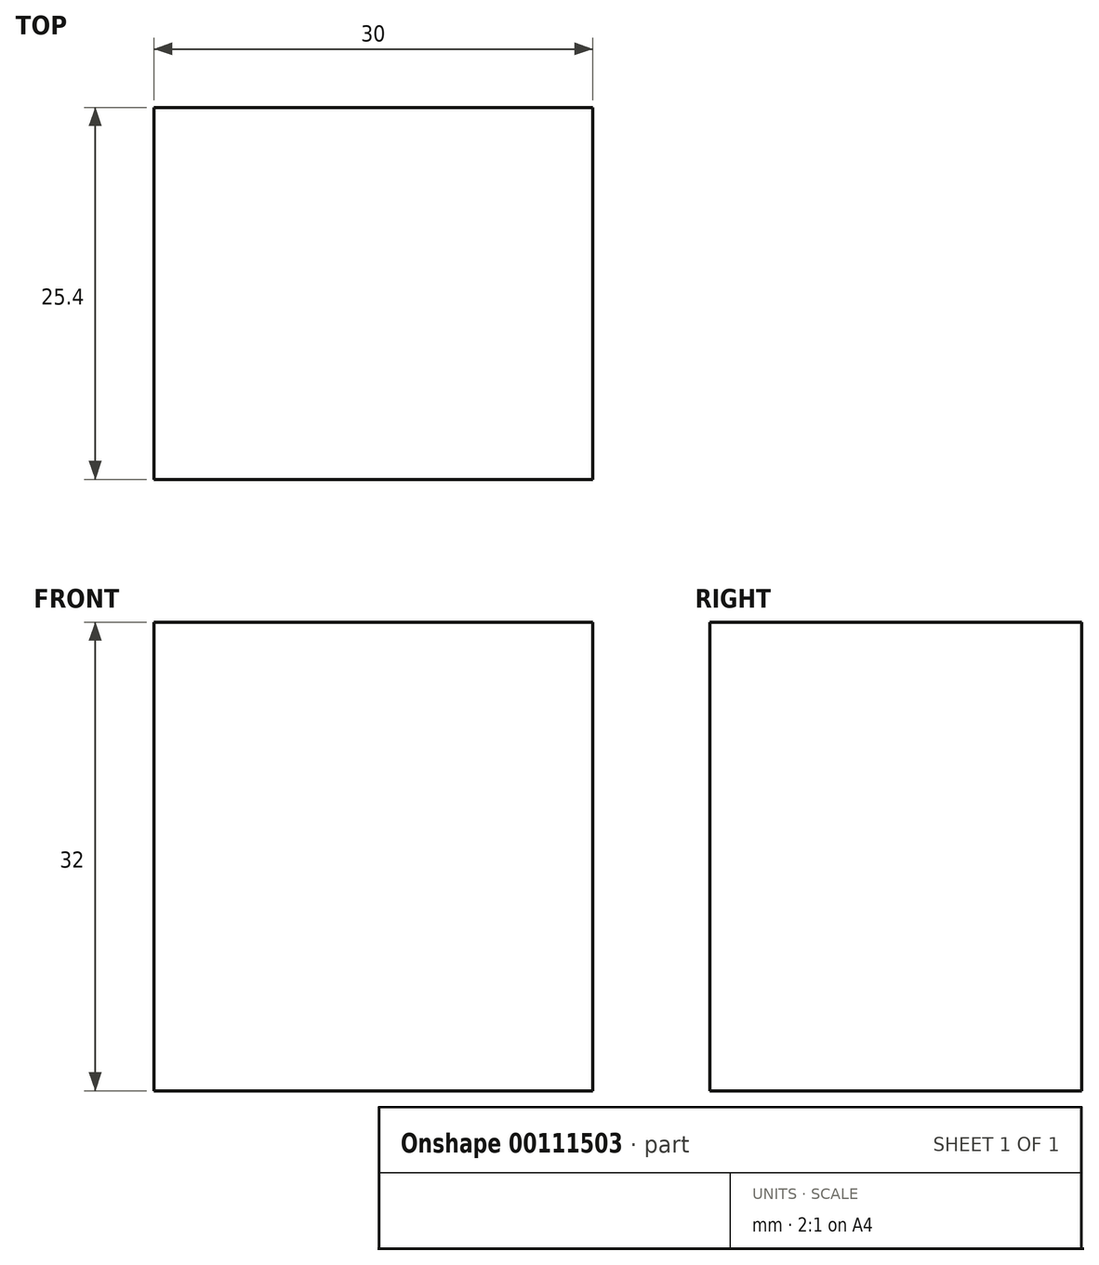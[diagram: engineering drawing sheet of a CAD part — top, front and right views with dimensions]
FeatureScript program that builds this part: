
annotation { "Feature Type Name" : "Feature", "Feature Type Description" : "" }
export const myFeature = defineFeature(function(context is Context, id is Id, definition is map)
    precondition{}
    {
        {
            var Q0;
            Q0=qCreatedBy(makeId("Front.planeOp"),FACE);
            var sketch = newSketch(context, id + "F0", { "sketchPlane" : qUnion([Q0])});
            skLineSegment(sketch, "E0.bottom", {"start": v(15, -16) * mm, "end": v(-15, -16) * mm});
            skLineSegment(sketch, "E0.top", {"start": v(15, 16) * mm, "end": v(-15, 16) * mm});
            skLineSegment(sketch, "E0.left", {"start": v(15, -16) * mm, "end": v(15, 16) * mm});
            skLineSegment(sketch, "E0.right", {"start": v(-15, -16) * mm, "end": v(-15, 16) * mm});
            skPoint(sketch, "E0.middle", {"position": v(0, 0) * mm});
            skSolve(sketch);
        }
        {
            var Q0;
            Q0 = qSketchRegion(id + "F0", true);
            extrude(context, id + "F1", {"entities" : qUnion([Q0]), "depth" : 25.4 * mm});
        }
    });
